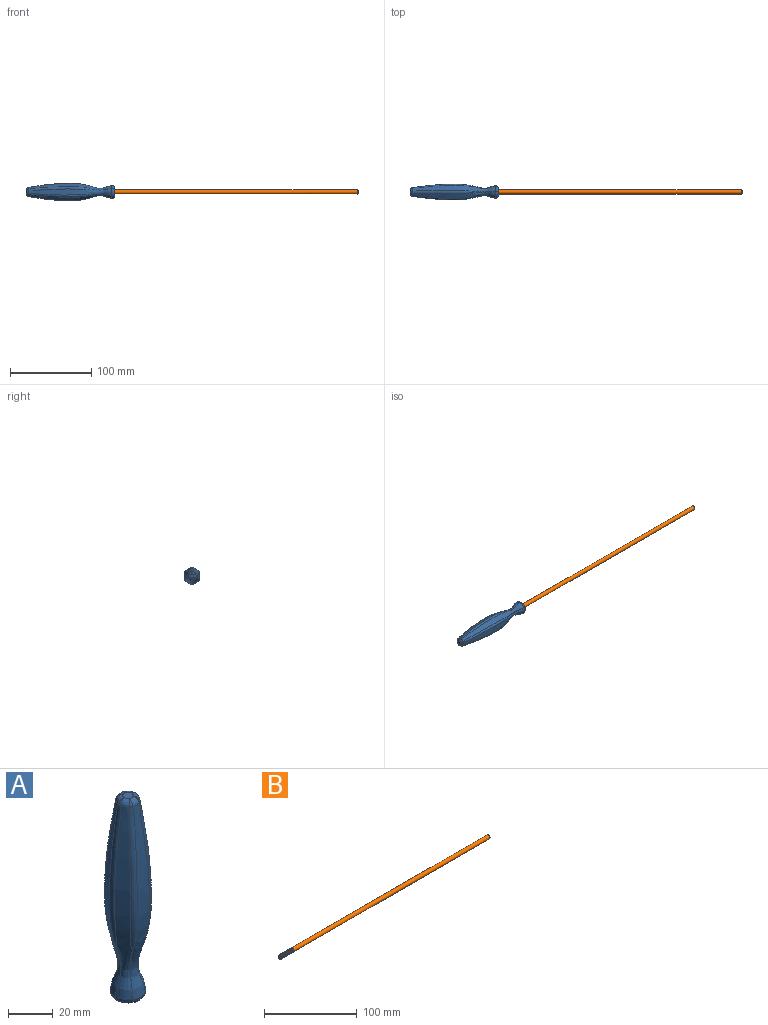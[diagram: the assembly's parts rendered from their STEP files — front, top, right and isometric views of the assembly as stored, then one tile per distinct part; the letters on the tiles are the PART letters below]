
ASSEMBLY  parts=2 mates=1
PART A: 46 faces, bbox 24x20.8x109 mm
  f0: plane 9.75x9.74mm, normal (0,0,-1), area 60.7mm2, adj f8,f9,f10,f11,f12,f13,f45
  f1: plane 5.06x4.74mm, normal (0,0,1), area 18.4mm2, adj f19,f20,f25,f26,f30,f31
  f2: bspline ~109x10.61mm, area 821mm2, adj f3,f7,f12,f24,f30,f33,f40,f41
  f3: bspline ~103.3x9.87mm, area 821mm2, adj f2,f4,f10,f27,f31,f33,f38,f39
  f4: bspline ~103.3x11.4mm, area 821mm2, adj f3,f5,f8,f21,f26,f27,f36,f37
  f5: bspline ~109x10.61mm, area 821mm2, adj f4,f6,f9,f16,f20,f21,f34,f35
  f6: bspline ~103.3x9.87mm, area 821mm2, adj f5,f7,f11,f14,f15,f16,f18,f19
  f7: bspline ~103.3x11.4mm, area 821mm2, adj f2,f6,f13,f14,f15,f18,f24,f25
  f8: bspline ~10.61x4.61mm, area 35.3mm2, adj f0,f4,f9,f10
  f9: bspline ~9.18x6.92mm, area 35.3mm2, adj f0,f5,f8,f11
  f10: bspline ~9.19x6.91mm, area 35.3mm2, adj f0,f3,f8,f12
  f11: bspline ~9.19x6.91mm, area 35.3mm2, adj f0,f6,f9,f13
  f12: bspline ~9.18x6.92mm, area 35.3mm2, adj f0,f2,f10,f13
  f13: bspline ~10.61x4.61mm, area 35.2mm2, adj f0,f7,f11,f12
  f14: bspline ~5x1.73mm, area 0mm2, adj f6,f7
  f15: bspline ~16x2.33mm, area 0mm2, adj f6,f7
  f16: bspline ~78.1x6.04mm, area 232mm2, adj f5,f6,f17
  f17: sphere r=3mm, area 3.5mm2, adj f16,f19,f20
  f18: bspline ~78.1x5.52mm, area 232mm2, adj f6,f7,f22
  f19: bspline ~4.89x4.43mm, area 15.4mm2, adj f1,f6,f17,f22
  f20: bspline ~4.89x4.4mm, area 15.4mm2, adj f1,f5,f17,f23
  f21: bspline ~78.1x5.53mm, area 232mm2, adj f4,f5,f23
  f22: sphere r=3mm, area 3.5mm2, adj f18,f19,f25
  f23: sphere r=3mm, area 3.1mm2, adj f20,f21,f26
  f24: bspline ~78.1x5.53mm, area 232mm2, adj f2,f7,f28
  f25: bspline ~5.07x3.24mm, area 15.4mm2, adj f1,f7,f22,f28
  f26: bspline ~5.07x3.24mm, area 15.4mm2, adj f1,f4,f23,f29
  f27: bspline ~78.1x5.52mm, area 232mm2, adj f3,f4,f29
  f28: sphere r=3mm, area 3.5mm2, adj f24,f25,f30
  f29: sphere r=3mm, area 3.6mm2, adj f26,f27,f31
  f30: bspline ~4.89x4.4mm, area 15.4mm2, adj f1,f2,f28,f32
  f31: bspline ~4.89x4.43mm, area 15.4mm2, adj f1,f3,f29,f32
  f32: sphere r=3mm, area 3.5mm2, adj f30,f31,f33
  f33: bspline ~78.1x6.04mm, area 232mm2, adj f2,f3,f32
  f34: bspline ~5x2mm, area 0mm2, adj f5,f6
  f35: bspline ~16x2.62mm, area 0mm2, adj f5,f6
  f36: bspline ~5x1.73mm, area 0mm2, adj f4,f5
  f37: bspline ~16x2.33mm, area 0mm2, adj f4,f5
  f38: bspline ~5x1.73mm, area 0mm2, adj f3,f4
  f39: bspline ~16x2.33mm, area 0mm2, adj f3,f4
  f40: bspline ~5x2mm, area 0mm2, adj f2,f3
  f41: bspline ~16x2.62mm, area 0mm2, adj f2,f3
  f42: bspline ~5x1.73mm, area 0mm2, adj f2,f7
  f43: bspline ~16x2.33mm, area 0mm2, adj f2,f7
  f44: cone r=0mm half-angle=59deg, axis (0,0,-1), area 16.2mm2, adj f45
  f45: cylinder r=2.1mm len=30mm, axis (0,0,-1), area 395.8mm2, adj f0,f44
PART B: 10 faces, bbox 320.6x5.1x5.8 mm
  f0: cone r=1.81mm half-angle=60deg, axis (-1,0,0), area 5mm2, adj f2,f3,f6,f8
  f1: cone r=2.5mm half-angle=45deg, axis (1,0,0), area 3.4mm2, adj f2,f3,f7,f8
  f2: bspline ~20.13x5.77mm, area 223.7mm2, adj f0,f1,f3,f7,f8
  f3: bspline ~20.13x5.77mm, area 224.2mm2, adj f0,f1,f2,f7,f8
  f4: cylinder r=2.5mm len=299mm, axis (-1,0,0), area 4696.7mm2, adj f6,f9
  f5: plane 3x3mm, normal (1,0,0), area 7.1mm2, adj f9
  f6: cone r=2.5mm half-angle=60deg, axis (1,0,0), area 10.8mm2, adj f0,f4
  f7: plane 4.07x3.89mm, normal (-1,0,0), area 12.2mm2, adj f1,f2,f3
  f8: cylinder r=2.41mm len=18.84mm, axis (-1,0,0), area -18.7mm2, adj f0,f1,f2,f3
  f9: cone r=1.5mm half-angle=45deg, axis (-1,0,0), area 17.8mm2, adj f4,f5
PLACE A rot(axis=(0,-1,0),90deg) t=(-61.35,28.68,-31.81)mm
PLACE B t=(-73.35,28.68,-31.81)mm
MATE fastened A.f44 <-> B.f0  axis (1,0,0) through (-53.35,28.68,-31.81)mm
